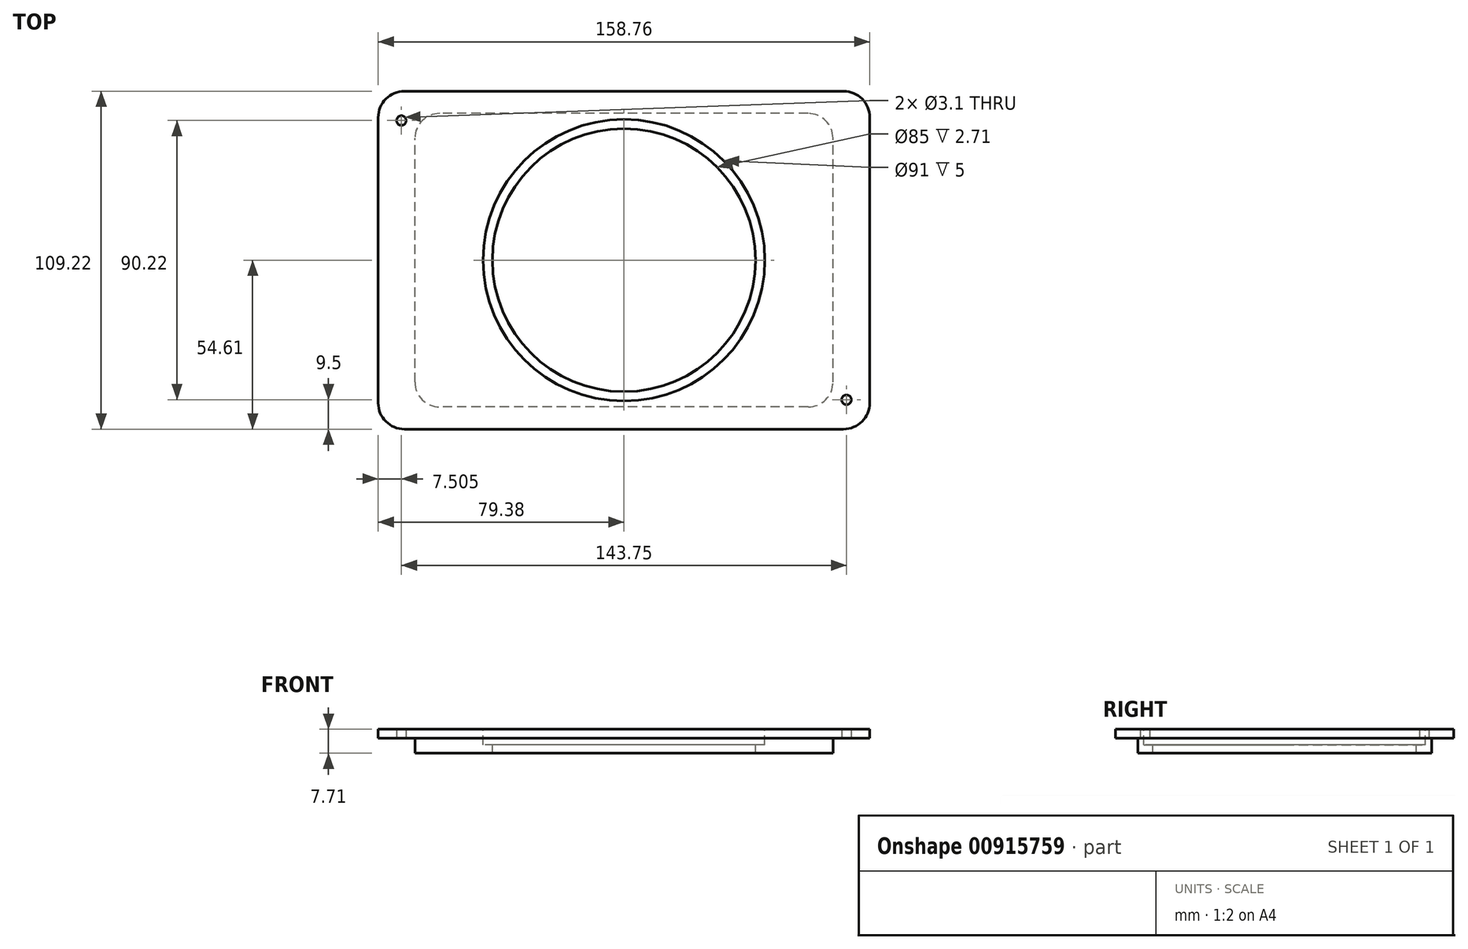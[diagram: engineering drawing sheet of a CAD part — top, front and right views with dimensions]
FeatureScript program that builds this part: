
annotation { "Feature Type Name" : "Feature", "Feature Type Description" : "" }
export const myFeature = defineFeature(function(context is Context, id is Id, definition is map)
    precondition{}
    {
        {
            var Q0;
            Q0=qCreatedBy(makeId("Top.planeOp"),FACE);
            var sketch = newSketch(context, id + "F0", { "sketchPlane" : qUnion([Q0])});
            skLineSegment(sketch, "E0.bottom", {"start": v(79.38, -54.61) * mm, "end": v(-79.38, -54.61) * mm});
            skLineSegment(sketch, "E0.top", {"start": v(79.37, 54.61) * mm, "end": v(-79.38, 54.6) * mm});
            skLineSegment(sketch, "E0.left", {"start": v(79.38, -54.61) * mm, "end": v(79.37, 54.61) * mm});
            skLineSegment(sketch, "E0.right", {"start": v(-79.37, -54.61) * mm, "end": v(-79.38, 54.6) * mm});
            skPoint(sketch, "E0.middle", {"position": v(0, 0) * mm});
            skCircle(sketch, "E1", {"center": v(71.88, -45.11) * mm, "radius": 1.55 * mm});
            skCircle(sketch, "E2", {"center": v(-71.88, 45.11) * mm, "radius": 1.55 * mm});
            skArc(sketch, "E3", {"start": v(79.37, 46.11) * mm, "mid": v(76.89, 52.12) * mm, "end": v(70.87, 54.61) * mm});
            skArc(sketch, "E4.MirrorCS", {"start": v(79.37, -46.11) * mm, "mid": v(76.89, -52.12) * mm, "end": v(70.87, -54.61) * mm});
            skArc(sketch, "E5.MirrorCS", {"start": v(-79.37, 46.11) * mm, "mid": v(-76.89, 52.12) * mm, "end": v(-70.87, 54.61) * mm});
            skArc(sketch, "E6.MirrorCS", {"start": v(-79.37, -46.11) * mm, "mid": v(-76.89, -52.12) * mm, "end": v(-70.87, -54.61) * mm});
            skSolve(sketch);
        }
        {
            var Q0;
            Q0=makeQuery(id+"F0.imprint","IMPRINT",FACE,{"disambiguationData":[TD([[makeQuery(id+"F0.imprint","IMPRINT",EDGE,{"derivedFrom":sQuery(id+"F0.wireOp",EDGE,"E1")}),-1.0]])]});
            extrude(context, id + "F1", {"entities" : qUnion([Q0]), "depth" : 2.91 * mm, "offsetDistance" : 25 * mm});
        }
        {
            var Q0;
            Q0=qCreatedBy(makeId("Top.planeOp"),FACE);
            var sketch = newSketch(context, id + "F2", { "sketchPlane" : qUnion([Q0])});
            skLineSegment(sketch, "E7.bottom", {"start": v(59.5, -47.42) * mm, "end": v(-59.5, -47.43) * mm});
            skLineSegment(sketch, "E7.top", {"start": v(59.5, 47.43) * mm, "end": v(-59.5, 47.42) * mm});
            skLineSegment(sketch, "E7.left", {"start": v(67.5, -39.42) * mm, "end": v(67.5, 39.43) * mm});
            skLineSegment(sketch, "E7.right", {"start": v(-67.5, -39.43) * mm, "end": v(-67.5, 39.42) * mm});
            skPoint(sketch, "E7.middle", {"position": v(0, 0) * mm});
            skPoint(sketch, "E8.visualSharp", {"position": v(-67.5, -47.43) * mm});
            skArc(sketch, "E8.filletArc", {"start": v(-67.5, -39.43) * mm, "mid": v(-65.16, -45.08) * mm, "end": v(-59.5, -47.43) * mm});
            skPoint(sketch, "E9.visualSharp", {"position": v(67.5, -47.42) * mm});
            skArc(sketch, "E9.filletArc", {"start": v(59.5, -47.42) * mm, "mid": v(65.16, -45.08) * mm, "end": v(67.5, -39.42) * mm});
            skPoint(sketch, "E10.visualSharp", {"position": v(-67.5, 47.42) * mm});
            skArc(sketch, "E10.filletArc", {"start": v(-59.5, 47.42) * mm, "mid": v(-65.16, 45.08) * mm, "end": v(-67.5, 39.42) * mm});
            skPoint(sketch, "E11.visualSharp", {"position": v(67.5, 47.43) * mm});
            skArc(sketch, "E11.filletArc", {"start": v(67.5, 39.43) * mm, "mid": v(65.16, 45.08) * mm, "end": v(59.5, 47.43) * mm});
            skSolve(sketch);
        }
        {
            var Q0;
            Q0=makeQuery(id+"F2.imprint","IMPRINT",FACE,{"disambiguationData":[TD([[makeQuery(id+"F2.imprint","IMPRINT",EDGE,{"derivedFrom":sQuery(id+"F2.wireOp",EDGE,"E7.bottom")}),-1.0]])]});
            extrude(context, id + "F3", {"entities" : qUnion([Q0]), "operationType" : NewBodyOperationType.ADD, "depth" : -4.8 * mm, "offsetDistance" : 25 * mm});
        }
        {
            var Q0;
            Q0=makeQuery(id+"F1.opExtrude","CAP_FACE",FACE,{"disambiguationData":[OSD([sQuery(id+"F0.wireOp",EDGE,"E0.bottom"),sQuery(id+"F0.wireOp",EDGE,"E0.top"),sQuery(id+"F0.wireOp",EDGE,"E0.left"),sQuery(id+"F0.wireOp",EDGE,"E0.right"),sQuery(id+"F0.wireOp",EDGE,"E1"),sQuery(id+"F0.wireOp",EDGE,"E2"),sQuery(id+"F0.wireOp",EDGE,"E3"),sQuery(id+"F0.wireOp",EDGE,"E4.MirrorCS"),sQuery(id+"F0.wireOp",EDGE,"E5.MirrorCS"),sQuery(id+"F0.wireOp",EDGE,"E6.MirrorCS")])],"isStart":false});
            var sketch = newSketch(context, id + "F4", { "sketchPlane" : qUnion([Q0])});
            skCircle(sketch, "E12", {"center": v(0, 0) * mm, "radius": 45.5 * mm});
            skCircle(sketch, "E13", {"center": v(0, 0) * mm, "radius": 42.5 * mm});
            skSolve(sketch);
        }
        {
            var Q0;
            Q0=makeQuery(id+"F4.imprint","IMPRINT",FACE,{"disambiguationData":[TD([[makeQuery(id+"F4.imprint","IMPRINT",EDGE,{"derivedFrom":sQuery(id+"F4.wireOp",EDGE,"E13")}),1.0]])]});
            extrude(context, id + "F5", {"entities" : qUnion([Q0]), "operationType" : NewBodyOperationType.REMOVE, "oppositeDirection" : true, "depth" : 25 * mm, "offsetDistance" : 25 * mm});
        }
        {
            var Q0;
            Q0 = qSketchRegion(id + "F4", true);
            extrude(context, id + "F6", {"entities" : qUnion([Q0]), "operationType" : NewBodyOperationType.REMOVE, "oppositeDirection" : true, "depth" : 5 * mm, "offsetDistance" : 25 * mm});
        }
    });
